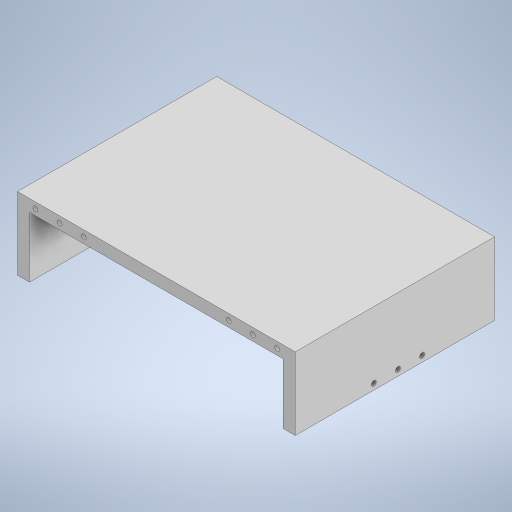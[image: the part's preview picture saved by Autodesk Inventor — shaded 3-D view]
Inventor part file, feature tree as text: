
AUTODESK INVENTOR PART (.ipt)
format: ipt  version: 2024 (Build 280153000, 153)  size: 256,512 bytes
history: native  units: in
note: dims shown in document units (in); Inventor stores cm internally (conversion verified against a paired STEP export)
features: hole x5, other x5, projected_geometry x3, extrude x2
ambient origin geometry x8: Origin, YZ Plane, XZ Plane, XY Plane, X Axis, Y Axis, Z Axis, Center Point
bodies: Solid1 (feature_tree)
feature tree (15):
  extrude  "TopBoxWidth"  Depth=8.25in TaperAngle=0.0deg
  extrude  "TrayCut"  Depth=3.0in
  hole  "FrontPlateHoles"  [1 undecoded]
  hole  "BackPlateHoles"  [1 undecoded]
  hole  "RightPlateHoles"  [1 undecoded]
  hole  "LeftPlateHoles"  [1 undecoded]
  other  "TopBoxFrame"
  other  "TrayShape"
  hole  "HoleGeometry"  [1 undecoded]
  projected_geometry  "Projected Loop1"
  projected_geometry  "Projected Loop2"
  other  "BackHoleGeo"
  projected_geometry  "Projected Loop3"
  other  "RightHoleGeo"
  other  "LeftHoleGeo"
note: 5 required parameter values undecoded (feature->parameter linkage not recoverable at this tier; creation-order binding heuristic only, values carry confidence <= 0.55)
